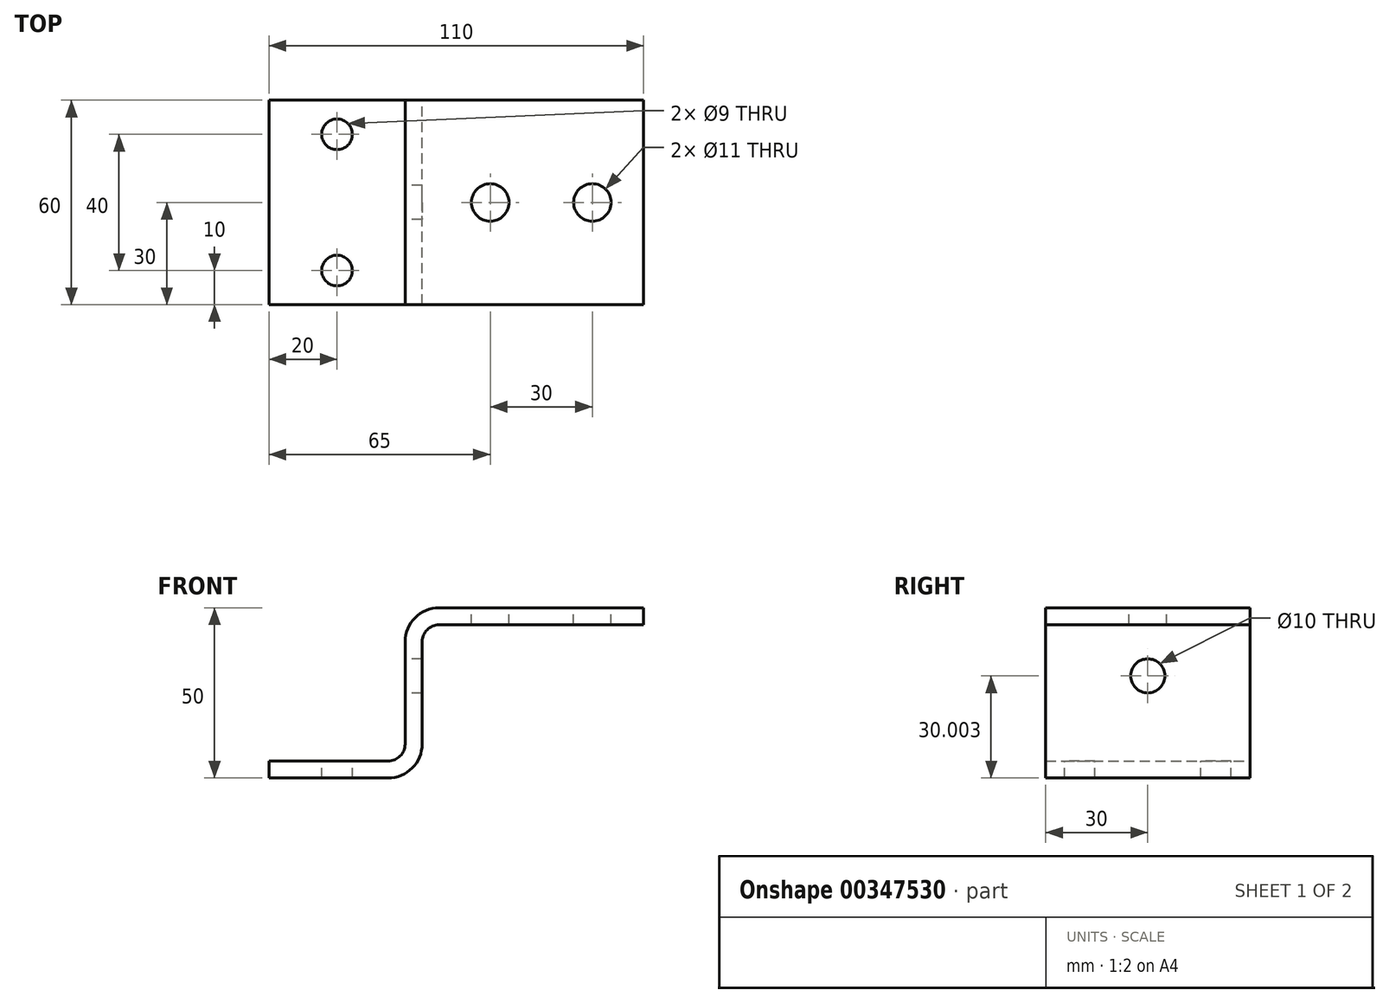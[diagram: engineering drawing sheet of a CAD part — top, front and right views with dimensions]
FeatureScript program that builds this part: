
annotation { "Feature Type Name" : "Feature", "Feature Type Description" : "" }
export const myFeature = defineFeature(function(context is Context, id is Id, definition is map)
    precondition{}
    {
        {
            var Q0;
            Q0=qCreatedBy(makeId("Front.planeOp"),FACE);
            var sketch = newSketch(context, id + "F0", { "sketchPlane" : qUnion([Q0])});
            skLineSegment(sketch, "E0", {"start": v(-110, 28.81) * mm, "end": v(-110, 33.81) * mm});
            skLineSegment(sketch, "E1", {"start": v(-110, 33.81) * mm, "end": v(-75, 33.81) * mm});
            skLineSegment(sketch, "E2", {"start": v(-70, 38.81) * mm, "end": v(-70, 68.81) * mm});
            skLineSegment(sketch, "E3", {"start": v(-60, 78.81) * mm, "end": v(0, 78.81) * mm});
            skLineSegment(sketch, "E4", {"start": v(0, 78.81) * mm, "end": v(0, 73.81) * mm});
            skLineSegment(sketch, "E5", {"start": v(0, 73.81) * mm, "end": v(-60, 73.81) * mm});
            skLineSegment(sketch, "E6", {"start": v(-65, 68.81) * mm, "end": v(-65, 38.81) * mm});
            skLineSegment(sketch, "E7", {"start": v(-75, 28.81) * mm, "end": v(-110, 28.81) * mm});
            skPoint(sketch, "E8.visualSharp", {"position": v(-70, 33.81) * mm});
            skArc(sketch, "E8.filletArc", {"start": v(-75, 33.81) * mm, "mid": v(-71.46, 35.28) * mm, "end": v(-70, 38.81) * mm});
            skPoint(sketch, "E9.visualSharp", {"position": v(-65, 73.81) * mm});
            skPoint(sketch, "E10.visualSharp", {"position": v(-65, 28.81) * mm});
            skArc(sketch, "E10.filletArc", {"start": v(-75, 28.81) * mm, "mid": v(-67.93, 31.74) * mm, "end": v(-65, 38.81) * mm});
            skPoint(sketch, "E11.visualSharp", {"position": v(-70, 78.81) * mm});
            skLineSegment(sketch, "E12", {"start": v(-70, 68.81) * mm, "end": v(-70, 78.81) * mm});
            skLineSegment(sketch, "E13", {"start": v(-60, 78.81) * mm, "end": v(-70, 78.81) * mm});
            skLineSegment(sketch, "E14", {"start": v(-60, 73.81) * mm, "end": v(-60, 73.81) * mm});
            skLineSegment(sketch, "E15", {"start": v(-65, 68.81) * mm, "end": v(-65, 68.81) * mm});
            skArc(sketch, "E16.filletArc", {"start": v(-60, 73.81) * mm, "mid": v(-63.54, 72.35) * mm, "end": v(-65, 68.81) * mm});
            skSolve(sketch);
        }
        {
            var Q0;
            Q0=makeQuery(id+"F0.imprint","IMPRINT",FACE,{"disambiguationData":[TD([[makeQuery(id+"F0.imprint","IMPRINT",EDGE,{"derivedFrom":sQuery(id+"F0.wireOp",EDGE,"E0")}),-1.0]])]});
            extrude(context, id + "F1", {"entities" : qUnion([Q0]), "depth" : 60 * mm});
        }
        {
            var Q0;
            Q0=makeQuery(id+"F1.opExtrude","SWEPT_FACE",FACE,{"disambiguationData":[OSD([sQuery(id+"F0.wireOp",EDGE,"E1")])]});
            var sketch = newSketch(context, id + "F2", { "sketchPlane" : qUnion([Q0])});
            skLineSegment(sketch, "E17", {"start": v(-110, 0) * mm, "end": v(-90, 0) * mm});
            skLineSegment(sketch, "E18", {"start": v(-90, 0) * mm, "end": v(-90, -10) * mm});
            skLineSegment(sketch, "E19", {"start": v(-110, -60) * mm, "end": v(-90, -60) * mm});
            skLineSegment(sketch, "E20", {"start": v(-90, -60) * mm, "end": v(-90, -50) * mm});
            skCircle(sketch, "E21", {"center": v(-90, -10) * mm, "radius": 4.5 * mm});
            skCircle(sketch, "E22", {"center": v(-90, -50) * mm, "radius": 4.5 * mm});
            skSolve(sketch);
        }
        {
            var Q0;
            Q0=sQuery(id+"F2.wireOp",VERTEX,"E18.end");
            var Q1;
            Q1=sQuery(id+"F2.wireOp",VERTEX,"E22.center");
            var Q2;
            Q2=makeQuery(id+"F1.opExtrude","SWEPT_BODY",BODY,{"disambiguationData":[OSD([sQuery(id+"F0.wireOp",EDGE,"E0"),sQuery(id+"F0.wireOp",EDGE,"E1"),sQuery(id+"F0.wireOp",EDGE,"E2"),sQuery(id+"F0.wireOp",EDGE,"E3"),sQuery(id+"F0.wireOp",EDGE,"E4"),sQuery(id+"F0.wireOp",EDGE,"E5"),sQuery(id+"F0.wireOp",EDGE,"E6"),sQuery(id+"F0.wireOp",EDGE,"E7"),sQuery(id+"F0.wireOp",EDGE,"E8.filletArc"),sQuery(id+"F0.wireOp",EDGE,"E9.filletArc"),sQuery(id+"F0.wireOp",EDGE,"E10.filletArc"),sQuery(id+"F0.wireOp",EDGE,"E11.filletArc")])]});
            hole(context, id + "F3", {"style" : HoleStyle.SIMPLE, "endStyle" : HoleEndStyle.BLIND, "holeDiameter" : 9 * mm, "holeDepth" : 50 * mm, "isTappedThrough" : true, "tappedDepth" : 12 * mm, "tapClearance" : 3, "startFromSketch" : true, "locations" : qUnion([Q0, Q1]), "scope" : qUnion([Q2])});
        }
        {
            var Q0;
            Q0=makeQuery(id+"F1.opExtrude","SWEPT_FACE",FACE,{"disambiguationData":[OSD([sQuery(id+"F0.wireOp",EDGE,"E2")])]});
            var sketch = newSketch(context, id + "F4", { "sketchPlane" : qUnion([Q0])});
            skLineSegment(sketch, "E23", {"start": v(60, 78.81) * mm, "end": v(60, 58.81) * mm});
            skLineSegment(sketch, "E24", {"start": v(60, 58.81) * mm, "end": v(30, 58.81) * mm});
            skCircle(sketch, "E25", {"center": v(30, 58.81) * mm, "radius": 5 * mm});
            skSolve(sketch);
        }
        {
            var Q0;
            Q0=sQuery(id+"F4.wireOp",VERTEX,"E25.center");
            var Q1;
            Q1=makeQuery(id+"F1.opExtrude","SWEPT_BODY",BODY,{"disambiguationData":[OSD([sQuery(id+"F0.wireOp",EDGE,"E0"),sQuery(id+"F0.wireOp",EDGE,"E1"),sQuery(id+"F0.wireOp",EDGE,"E2"),sQuery(id+"F0.wireOp",EDGE,"E3"),sQuery(id+"F0.wireOp",EDGE,"E4"),sQuery(id+"F0.wireOp",EDGE,"E5"),sQuery(id+"F0.wireOp",EDGE,"E6"),sQuery(id+"F0.wireOp",EDGE,"E7"),sQuery(id+"F0.wireOp",EDGE,"E8.filletArc"),sQuery(id+"F0.wireOp",EDGE,"E10.filletArc"),sQuery(id+"F0.wireOp",EDGE,"E12"),sQuery(id+"F0.wireOp",EDGE,"E13"),sQuery(id+"F0.wireOp",EDGE,"E14"),sQuery(id+"F0.wireOp",EDGE,"E15")])]});
            hole(context, id + "F5", {"style" : HoleStyle.SIMPLE, "endStyle" : HoleEndStyle.BLIND, "holeDiameter" : 10 * mm, "holeDepth" : 50 * mm, "isTappedThrough" : true, "tappedDepth" : 12 * mm, "tapClearance" : 3, "startFromSketch" : true, "locations" : qUnion([Q0]), "scope" : qUnion([Q1])});
        }
        {
            var Q0;
            Q0=makeQuery(id+"F1.opExtrude","SWEPT_EDGE",EDGE,{"disambiguationData":[OSD([sQuery(id+"F0.wireOp",EDGE,"E12"),sQuery(id+"F0.wireOp",EDGE,"E13")])]});
            fillet(context, id + "F6", {"entities" : qUnion([Q0]), "radius" : 10 * mm, "tangentPropagation" : true, "allowEdgeOverflow" : false});
        }
        {
            var Q0;
            Q0=makeQuery(id+"F1.opExtrude","SWEPT_FACE",FACE,{"disambiguationData":[OSD([sQuery(id+"F0.wireOp",EDGE,"E3"),sQuery(id+"F0.wireOp",EDGE,"E13")])]});
            var sketch = newSketch(context, id + "F7", { "sketchPlane" : qUnion([Q0])});
            skLineSegment(sketch, "E26", {"start": v(0, 0) * mm, "end": v(0, -30) * mm});
            skLineSegment(sketch, "E27", {"start": v(0, -30) * mm, "end": v(-15, -30) * mm});
            skLineSegment(sketch, "E28", {"start": v(-15, -30) * mm, "end": v(-45, -30) * mm});
            skCircle(sketch, "E29", {"center": v(-15, -30) * mm, "radius": 5.5 * mm});
            skCircle(sketch, "E30", {"center": v(-45, -30) * mm, "radius": 5.5 * mm});
            skSolve(sketch);
        }
        {
            var Q0;
            Q0=sQuery(id+"F7.wireOp",VERTEX,"E29.center");
            var Q1;
            Q1=sQuery(id+"F7.wireOp",VERTEX,"E28.end");
            var Q2;
            Q2=makeQuery(id+"F1.opExtrude","SWEPT_BODY",BODY,{"disambiguationData":[OSD([sQuery(id+"F0.wireOp",EDGE,"E0"),sQuery(id+"F0.wireOp",EDGE,"E1"),sQuery(id+"F0.wireOp",EDGE,"E2"),sQuery(id+"F0.wireOp",EDGE,"E3"),sQuery(id+"F0.wireOp",EDGE,"E4"),sQuery(id+"F0.wireOp",EDGE,"E5"),sQuery(id+"F0.wireOp",EDGE,"E6"),sQuery(id+"F0.wireOp",EDGE,"E7"),sQuery(id+"F0.wireOp",EDGE,"E8.filletArc"),sQuery(id+"F0.wireOp",EDGE,"E10.filletArc"),sQuery(id+"F0.wireOp",EDGE,"E12"),sQuery(id+"F0.wireOp",EDGE,"E13"),sQuery(id+"F0.wireOp",EDGE,"E16.filletArc")])]});
            hole(context, id + "F8", {"style" : HoleStyle.SIMPLE, "endStyle" : HoleEndStyle.BLIND, "holeDiameter" : 11 * mm, "holeDepth" : 50 * mm, "isTappedThrough" : true, "tappedDepth" : 12 * mm, "tapClearance" : 3, "startFromSketch" : true, "locations" : qUnion([Q0, Q1]), "scope" : qUnion([Q2])});
        }
    });
